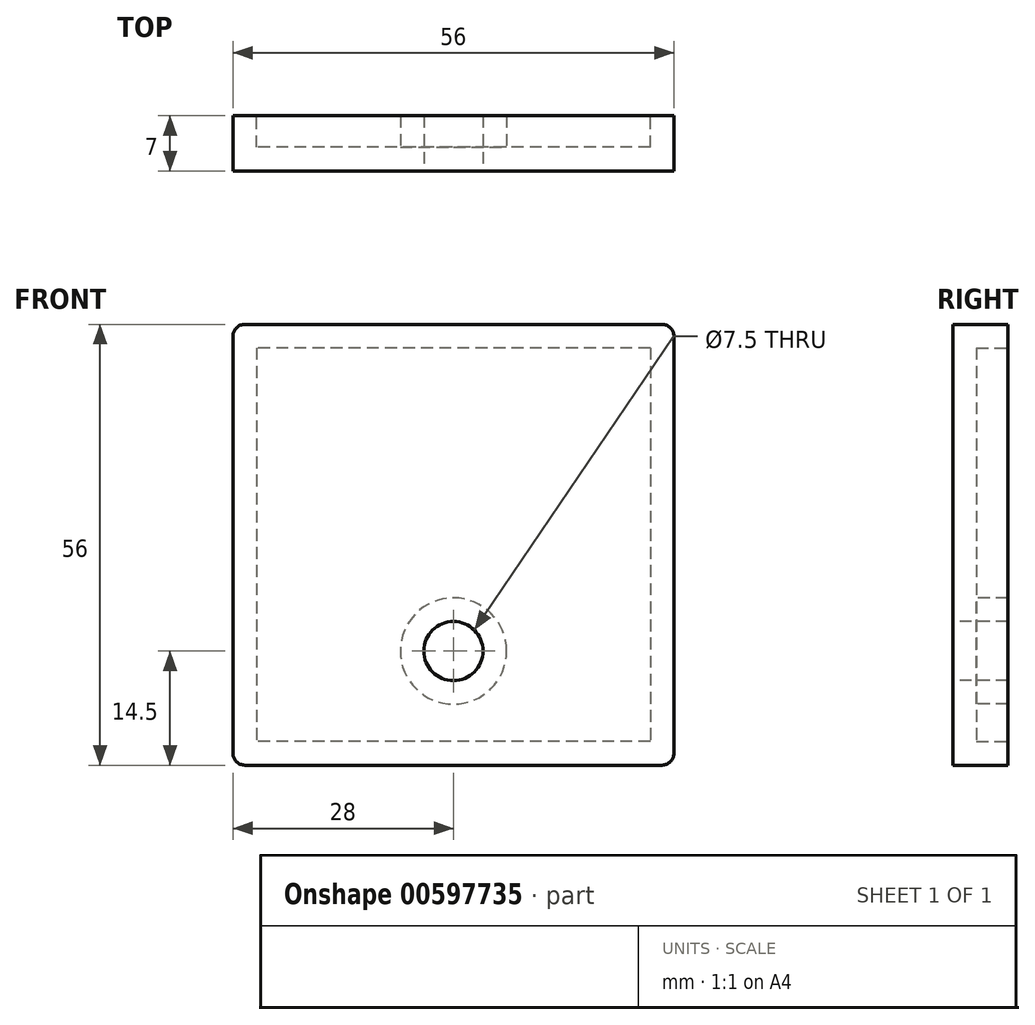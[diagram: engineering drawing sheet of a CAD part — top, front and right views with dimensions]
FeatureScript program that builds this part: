
annotation { "Feature Type Name" : "Feature", "Feature Type Description" : "" }
export const myFeature = defineFeature(function(context is Context, id is Id, definition is map)
    precondition{}
    {
        {
            var Q0;
            Q0=qCreatedBy(makeId("Front.planeOp"),FACE);
            var sketch = newSketch(context, id + "F0", { "sketchPlane" : qUnion([Q0])});
            skLineSegment(sketch, "E0.bottom", {"start": v(26.5, 28) * mm, "end": v(-26.5, 28) * mm});
            skLineSegment(sketch, "E0.top", {"start": v(26.5, -28) * mm, "end": v(-26.5, -28) * mm});
            skLineSegment(sketch, "E0.left", {"start": v(28, 26.5) * mm, "end": v(28, -26.5) * mm});
            skLineSegment(sketch, "E0.right", {"start": v(-28, 26.5) * mm, "end": v(-28, -26.5) * mm});
            skPoint(sketch, "E0.middle", {"position": v(0, 0) * mm});
            skPoint(sketch, "E1.visualSharp", {"position": v(-28, 28) * mm});
            skArc(sketch, "E1.filletArc", {"start": v(-26.5, 28) * mm, "mid": v(-27.56, 27.56) * mm, "end": v(-28, 26.5) * mm});
            skPoint(sketch, "E2.visualSharp", {"position": v(28, 28) * mm});
            skArc(sketch, "E2.filletArc", {"start": v(28, 26.5) * mm, "mid": v(27.56, 27.56) * mm, "end": v(26.5, 28) * mm});
            skPoint(sketch, "E3.visualSharp", {"position": v(-28, -28) * mm});
            skArc(sketch, "E3.filletArc", {"start": v(-28, -26.5) * mm, "mid": v(-27.56, -27.56) * mm, "end": v(-26.5, -28) * mm});
            skPoint(sketch, "E4.visualSharp", {"position": v(28, -28) * mm});
            skArc(sketch, "E4.filletArc", {"start": v(26.5, -28) * mm, "mid": v(27.56, -27.56) * mm, "end": v(28, -26.5) * mm});
            skSolve(sketch);
        }
        {
            var Q0;
            Q0=makeQuery(id+"F0.imprint","IMPRINT",FACE,{"disambiguationData":[TD([[makeQuery(id+"F0.imprint","IMPRINT",EDGE,{"derivedFrom":sQuery(id+"F0.wireOp",EDGE,"E0.bottom")}),1.0]])]});
            extrude(context, id + "F1", {"entities" : qUnion([Q0]), "depth" : 7 * mm, "offsetDistance" : 25 * mm});
        }
        {
            var Q0;
            Q0=makeQuery(id+"F1.opExtrude","CAP_FACE",FACE,{"disambiguationData":[OSD([sQuery(id+"F0.wireOp",EDGE,"E0.bottom"),sQuery(id+"F0.wireOp",EDGE,"E0.top"),sQuery(id+"F0.wireOp",EDGE,"E0.left"),sQuery(id+"F0.wireOp",EDGE,"E0.right"),sQuery(id+"F0.wireOp",EDGE,"E1.filletArc"),sQuery(id+"F0.wireOp",EDGE,"E2.filletArc"),sQuery(id+"F0.wireOp",EDGE,"E3.filletArc"),sQuery(id+"F0.wireOp",EDGE,"E4.filletArc")])],"isStart":false});
            var sketch = newSketch(context, id + "F2", { "sketchPlane" : qUnion([Q0])});
            skCircle(sketch, "E5", {"center": v(0, -13.5) * mm, "radius": 3.75 * mm});
            skSolve(sketch);
        }
        {
            var Q0;
            Q0 = qSketchRegion(id + "F2", true);
            extrude(context, id + "F3", {"entities" : qUnion([Q0]), "operationType" : NewBodyOperationType.REMOVE, "oppositeDirection" : true, "depth" : 7 * mm, "offsetDistance" : 25 * mm});
        }
        {
            var Q0;
            Q0=makeQuery(id+"F1.opExtrude","CAP_FACE",FACE,{"disambiguationData":[OSD([sQuery(id+"F0.wireOp",EDGE,"E0.bottom"),sQuery(id+"F0.wireOp",EDGE,"E0.top"),sQuery(id+"F0.wireOp",EDGE,"E0.left"),sQuery(id+"F0.wireOp",EDGE,"E0.right"),sQuery(id+"F0.wireOp",EDGE,"E1.filletArc"),sQuery(id+"F0.wireOp",EDGE,"E2.filletArc"),sQuery(id+"F0.wireOp",EDGE,"E3.filletArc"),sQuery(id+"F0.wireOp",EDGE,"E4.filletArc")])],"isStart":true});
            shell(context, id + "F4", {"entities" : qUnion([Q0]), "thickness" : 3 * mm});
        }
    });
